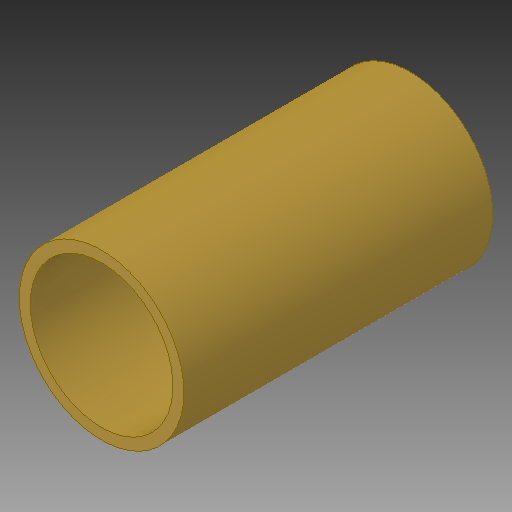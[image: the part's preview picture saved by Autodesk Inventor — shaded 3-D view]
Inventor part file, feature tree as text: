
AUTODESK INVENTOR PART (.ipt)
format: ipt  version: 2019 (Build 230136000, 136)  size: 105,984 bytes
history: native  units: in
note: dims shown in document units (in); Inventor stores cm internally (conversion verified against a paired STEP export)
features: revolve x1
ambient origin geometry x8: Origin, YZ Plane, XZ Plane, XY Plane, X Axis, Y Axis, Z Axis, Center Point
bodies: Solid1 (feature_tree)
feature tree (1):
  revolve  "Revolve1"  [1 undecoded]
note: 1 required parameter value undecoded (feature->parameter linkage not recoverable at this tier; creation-order binding heuristic only, values carry confidence <= 0.55)
